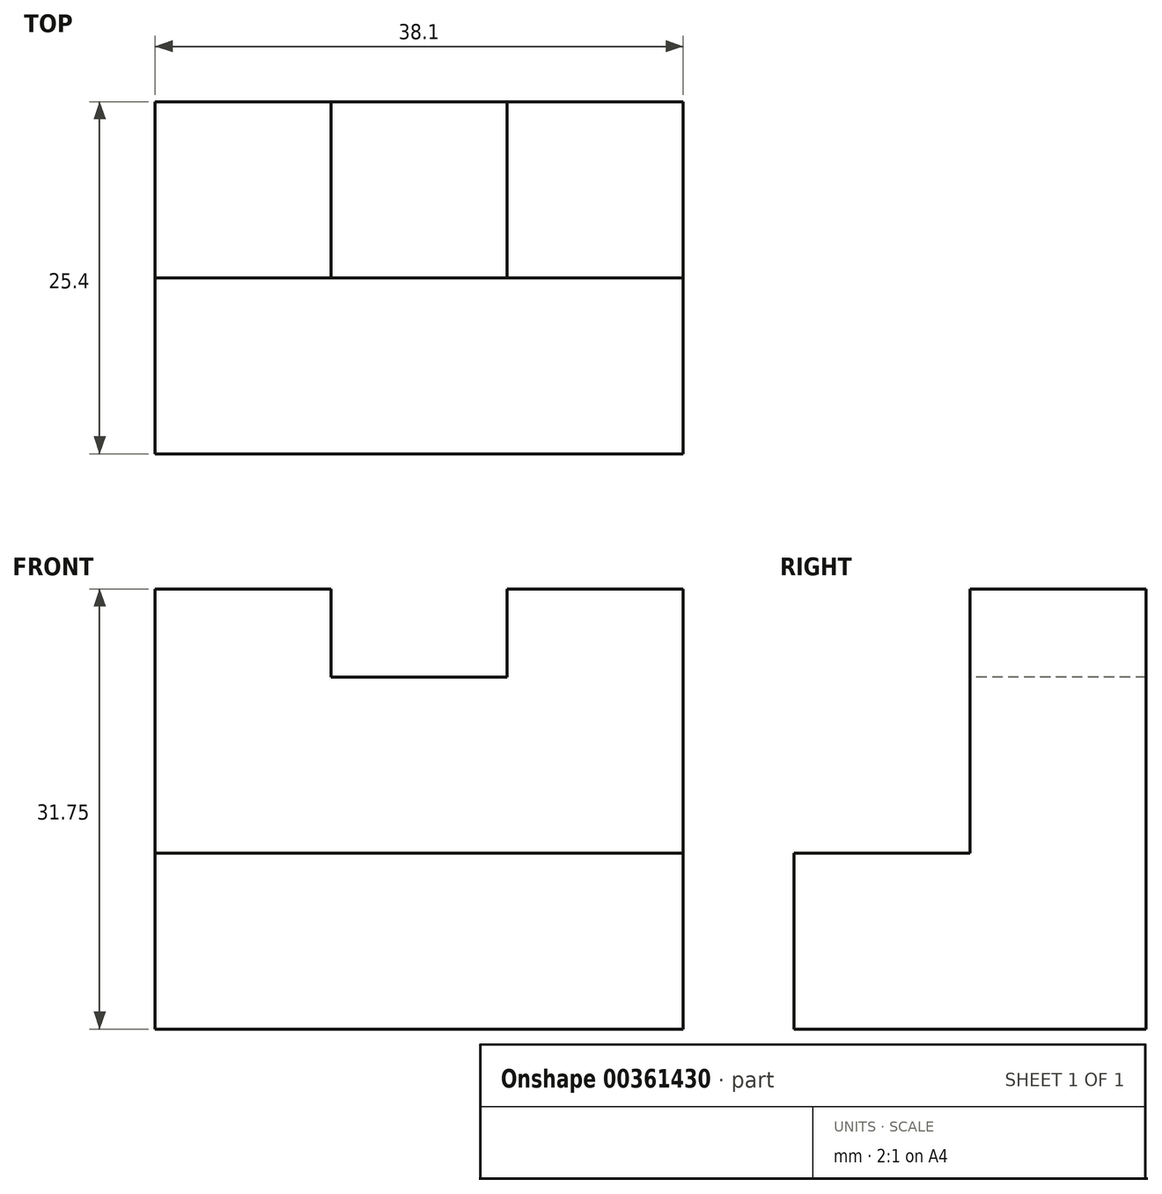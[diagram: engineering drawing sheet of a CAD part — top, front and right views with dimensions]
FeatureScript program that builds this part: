
annotation { "Feature Type Name" : "Feature", "Feature Type Description" : "" }
export const myFeature = defineFeature(function(context is Context, id is Id, definition is map)
    precondition{}
    {
        {
            var Q0;
            Q0=qCreatedBy(makeId("Right.planeOp"),FACE);
            var sketch = newSketch(context, id + "F0", { "sketchPlane" : qUnion([Q0])});
            skLineSegment(sketch, "E0", {"start": v(0, 0) * mm, "end": v(0, 31.75) * mm});
            skLineSegment(sketch, "E1", {"start": v(0, 0) * mm, "end": v(-25.4, 0) * mm});
            skLineSegment(sketch, "E2", {"start": v(-25.4, 0) * mm, "end": v(-25.4, 12.7) * mm});
            skLineSegment(sketch, "E3", {"start": v(-25.4, 12.7) * mm, "end": v(-12.7, 12.7) * mm});
            skLineSegment(sketch, "E4", {"start": v(-12.7, 12.7) * mm, "end": v(-12.7, 31.75) * mm});
            skLineSegment(sketch, "E5", {"start": v(-12.7, 31.75) * mm, "end": v(0, 31.75) * mm});
            skSolve(sketch);
        }
        {
            var Q0;
            Q0=makeQuery(id+"F0.imprint","IMPRINT",FACE,{"disambiguationData":[TD([[makeQuery(id+"F0.imprint","IMPRINT",EDGE,{"derivedFrom":sQuery(id+"F0.wireOp",EDGE,"E0")}),1.0]])]});
            extrude(context, id + "F1", {"entities" : qUnion([Q0]), "depth" : 38.1 * mm});
        }
        {
            var Q0;
            Q0=makeQuery(id+"F1.opExtrude","SWEPT_FACE",FACE,{"disambiguationData":[OSD([sQuery(id+"F0.wireOp",EDGE,"E5")])]});
            var sketch = newSketch(context, id + "F2", { "sketchPlane" : qUnion([Q0])});
            skLineSegment(sketch, "E6", {"start": v(0, 0) * mm, "end": v(12.7, 0) * mm});
            skLineSegment(sketch, "E7", {"start": v(12.7, 0) * mm, "end": v(12.7, -12.7) * mm});
            skLineSegment(sketch, "E8", {"start": v(12.7, -12.7) * mm, "end": v(25.4, -12.7) * mm});
            skLineSegment(sketch, "E9", {"start": v(25.4, -12.7) * mm, "end": v(25.4, 0) * mm});
            skLineSegment(sketch, "E10", {"start": v(25.4, 0) * mm, "end": v(12.7, 0) * mm});
            skSolve(sketch);
        }
        {
            var Q0;
            Q0 = qSketchRegion(id + "F2", true);
            extrude(context, id + "F3", {"entities" : qUnion([Q0]), "operationType" : NewBodyOperationType.REMOVE, "oppositeDirection" : true, "depth" : 6.35 * mm});
        }
    });
